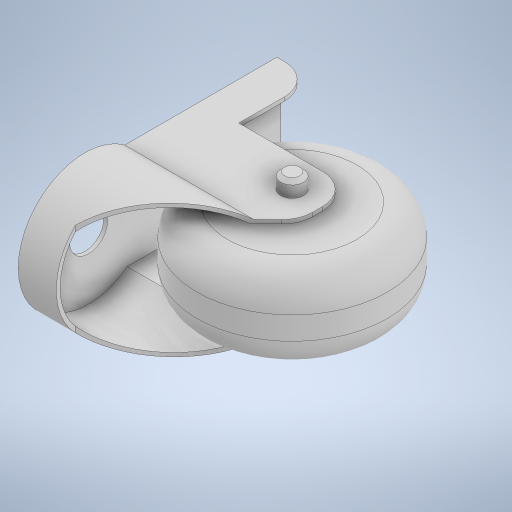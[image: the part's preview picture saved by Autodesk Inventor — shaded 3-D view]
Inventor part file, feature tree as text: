
AUTODESK INVENTOR PART (.ipt)
format: ipt  version: 2023 (Build 270158000, 158)  size: 410,112 bytes
history: native  units: mm
features: sketch x9, extrude x8, fillet x4, other x3, chamfer x1
ambient origin geometry x8: Origin, YZ Plane, XZ Plane, XY Plane, X Axis, Y Axis, Z Axis, Center Point
bodies: Body1 (feature_tree)
feature tree (25):
  other  "Твердое тело1"
  sketch  "Эскиз1"
  extrude  "Выдавливание1"  Depth=68.0mm
  extrude  "Выдавливание2"  Depth=10.0mm
  other  "РабПлоскость1"
  extrude  "Выдавливание3"  Depth=20.0mm
  extrude  "Выдавливание4"  Depth=30.0mm
  extrude  "Выдавливание5"  Depth=5.0mm
  fillet  "Сопряжение1"  Radius=14.0mm
  fillet  "Сопряжение2"  Radius=28.0mm
  fillet  "Сопряжение3"  Radius=35.0mm
  extrude  "Выдавливание6"  Depth=40.0mm TaperAngle=0.0deg
  extrude  "Выдавливание7"  Depth=23.25mm
  other  "РабПлоскость2"
  extrude  "Выдавливание8"  Depth=10.0mm
  fillet  "Сопряжение4"  Radius=20.0mm
  chamfer  "Фаска1"  Distance=30.0mm
  sketch  "Эскиз2"
  sketch  "Эскиз3"
  sketch  "Эскиз4"
  sketch  "Эскиз5"
  sketch  "Эскиз6"
  sketch  "Эскиз7"
  sketch  "Эскиз8"
  sketch  "Эскиз9"
